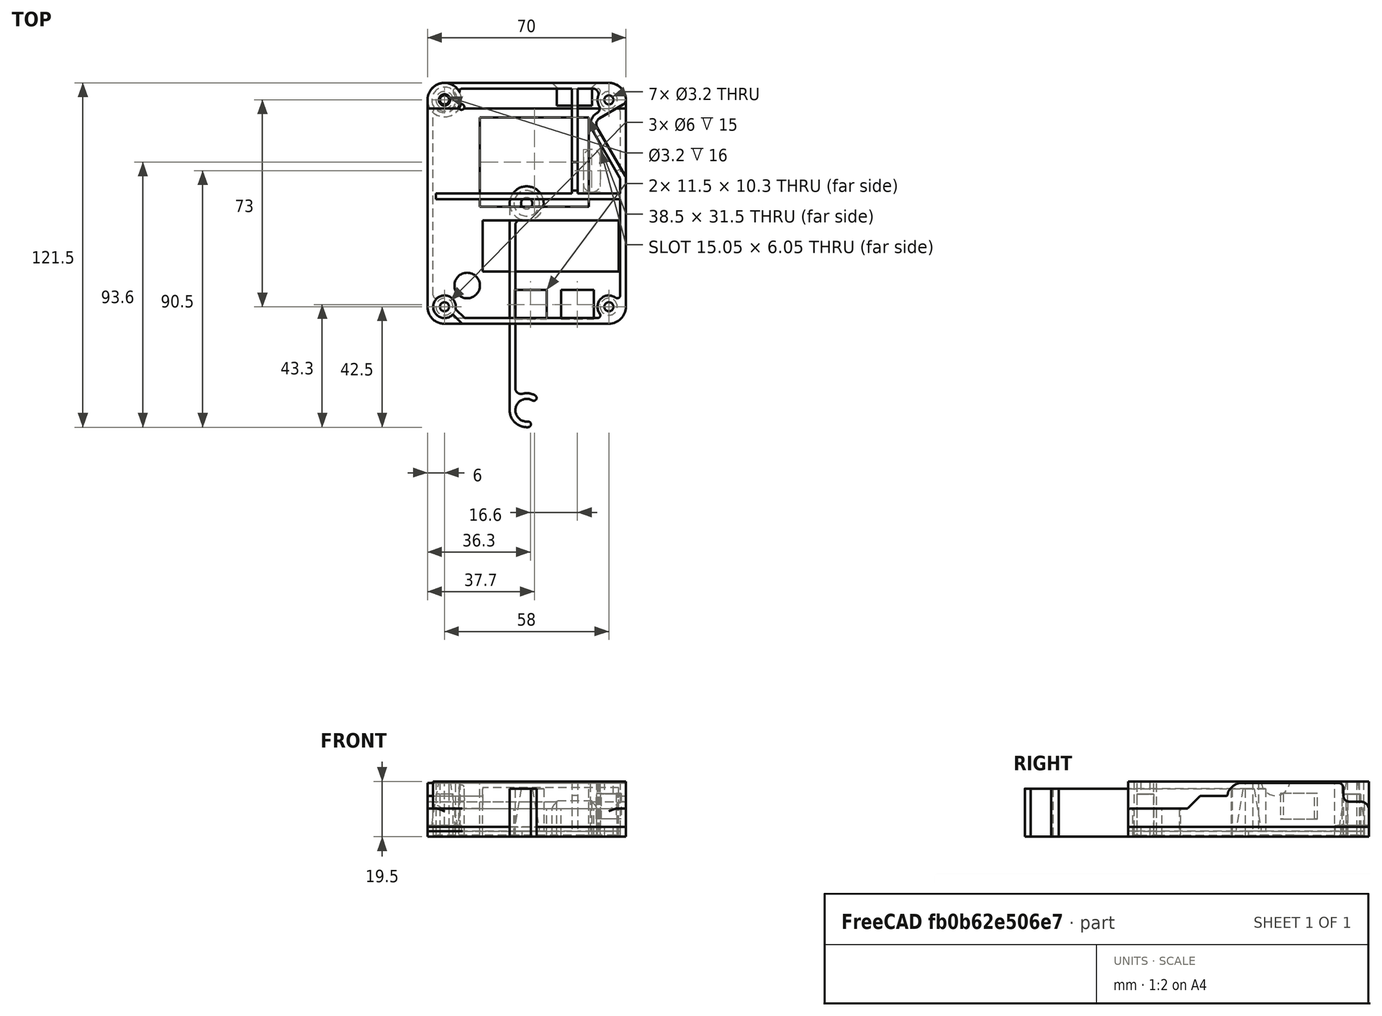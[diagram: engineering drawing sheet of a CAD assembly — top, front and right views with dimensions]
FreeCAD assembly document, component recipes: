
FREECAD ASSEMBLY — COMPONENT RECIPES ("GM328TesterCase")

This assembly document has 4 components, labeled P0..P3 below (a component is one placed body or linked part). 4 of them carry a construction recipe — the FreeCAD feature program that regenerates the part from scratch, quoted from this document or its linked companion documents; the rest are supplied as boundary geometry only. No exploded tour is included for this assembly.
COMPONENT P0 — recipe-attached ("Middle", modeled in this document).
Construction recipe (the document's own serialized feature program — sketch geometry with constraints, then the solid features built on it; lengths are millimeters unless a unit is written):

FEATURE [Sketcher::SketchObject] Sketch
  ArcFitTolerance = 1e-06
  AttachmentSupport = -> [XY_Plane]
  FullyConstrained = true
  MakeInternals = false
  MapMode = 5
  expr: Constraints[19] = <<Spreadsheet>>.OuterLength
  expr: Constraints[20] = <<Spreadsheet>>.OuterWidth
  expr: Constraints[21] = <<Spreadsheet>>.OuterCornerRadius
  expr: Constraints[29] = <<Spreadsheet>>.ThroughHole3
  sketch-geometry (18):
    g0: LineSegment StartX=-35 StartY=36.5 StartZ=0 EndX=-35 EndY=-36.5 EndZ=0
    g1: LineSegment StartX=-29 StartY=-42.5 StartZ=0 EndX=29 EndY=-42.5 EndZ=0
    g2: LineSegment StartX=35 StartY=-36.5 StartZ=0 EndX=35 EndY=36.5 EndZ=0
    g3: LineSegment StartX=29 StartY=42.5 StartZ=0 EndX=-29 EndY=42.5 EndZ=0
    g4: ArcOfCircle CenterX=-29 CenterY=36.5 CenterZ=0 NormalX=0 NormalY=0 NormalZ=1 AngleXU=0 Radius=6 StartAngle=1.5708 EndAngle=3.14159
    g5: ArcOfCircle CenterX=-29 CenterY=-36.5 CenterZ=0 NormalX=0 NormalY=0 NormalZ=1 AngleXU=0 Radius=6 StartAngle=3.14159 EndAngle=4.71239
    g6: ArcOfCircle CenterX=29 CenterY=-36.5 CenterZ=0 NormalX=0 NormalY=0 NormalZ=1 AngleXU=0 Radius=6 StartAngle=4.71239 EndAngle=6.28319
    g7: ArcOfCircle CenterX=29 CenterY=36.5 CenterZ=0 NormalX=0 NormalY=0 NormalZ=1 AngleXU=0 Radius=6 StartAngle=3e-16 EndAngle=1.5708
    g8: GeomPoint [constr] X=-35 Y=42.5 Z=0
    g9: GeomPoint [constr] X=35 Y=-42.5 Z=0
    g10: Circle CenterX=29 CenterY=36.5 CenterZ=0 NormalX=0 NormalY=0 NormalZ=1 AngleXU=0 Radius=1.6
    g11: Circle CenterX=-29 CenterY=36.5 CenterZ=0 NormalX=0 NormalY=0 NormalZ=1 AngleXU=0 Radius=1.6
    g12: Circle CenterX=-29 CenterY=-36.5 CenterZ=0 NormalX=0 NormalY=0 NormalZ=1 AngleXU=0 Radius=1.6
    g13: Circle CenterX=29 CenterY=-36.5 CenterZ=0 NormalX=0 NormalY=0 NormalZ=1 AngleXU=0 Radius=1.6
    g14: ArcOfCircle CenterX=23 CenterY=16 CenterZ=0 NormalX=0 NormalY=0 NormalZ=1 AngleXU=0 Radius=3.02394 StartAngle=3e-16 EndAngle=3.14159
    g15: ArcOfCircle CenterX=23 CenterY=7 CenterZ=0 NormalX=0 NormalY=0 NormalZ=1 AngleXU=0 Radius=3.02394 StartAngle=3.14159 EndAngle=6.28319
    g16: LineSegment StartX=26.0239 StartY=16 StartZ=0 EndX=26.0239 EndY=7 EndZ=0
    g17: LineSegment StartX=19.9761 StartY=16 StartZ=0 EndX=19.9761 EndY=7 EndZ=0
  constraints (40):
    c: Tangent(g0,g4) = -1.5708
    c: Tangent(g0,g5) = -1.5708
    c: Tangent(g1,g5) = -1.5708
    c: Tangent(g1,g6) = -1.5708
    c: Tangent(g2,g6) = -1.5708
    c: Tangent(g2,g7) = -1.5708
    c: Tangent(g3,g7) = -1.5708
    c: Tangent(g3,g4) = -1.5708
    c: Vertical(g2)
    c: Horizontal(g1)
    c: Equal(g4,g5)
    c: Equal(g5,g6)
    c: Equal(g6,g7)
    c: PointOnObject(g8,g0)
    c: PointOnObject(g8,g3)
    c: PointOnObject(g9,g1)
    c: PointOnObject(g9,g2)
    c: Symmetric(g3,g3,g-2)
    c: Symmetric(g0,g0,g-1)
    c: DistanceY(g1,g3) = 85
    c: DistanceX(g0,g2) = 70
    c: Radius(g7) = 6
    c: Coincident(g10,g7)
    c: Coincident(g11,g4)
    c: Coincident(g12,g5)
    c: Coincident(g13,g6)
    c: Equal(g13,g12)
    c: Equal(g12,g10)
    c: Equal(g10,g11)
    c: Diameter(g10) = 3.2
    c: Tangent(g14,g16) = 1.5708
    c: Tangent(g14,g17) = -1.5708
    c: Tangent(g15,g16) = 1.5708
    c: Tangent(g15,g17) = -1.5708
    c: Equal(g14,g15)
    c: Vertical(g17)
    c: Distance(g14) = 9.5
    c: DistanceY(g15,g14) = 9
    c: DistanceY(g15) = 7
    c: DistanceX(g15) = 23
FEATURE [PartDesign::Pad] Pad
  Direction = (0,0,1)
  Length = 3.5
  Length2 = 10
  Profile = -> Sketch
  ReferenceAxis = -> Sketch [N_Axis]
  Refine = true
  Suppressed = false
  Type = 0
FEATURE [Sketcher::SketchObject] Sketch001
  ArcFitTolerance = 1e-06
  AttachmentSupport = -> [Pad]
  ExternalGeometry = -> [Pad]
  FullyConstrained = true
  MakeInternals = false
  MapMode = 5
  Placement = pos=(0,0,3.5) rot=(0,0,1;0rad)
  expr: Constraints[33] = <<Spreadsheet>>.WallThickness
  expr: Constraints[34] = <<Spreadsheet>>.WallThickness
  expr: Constraints[35] = <<Spreadsheet>>.ScrewPostSmallRadius
  expr: Constraints[36] = <<Spreadsheet>>.ScrewPostDiameter / 2
  sketch-geometry (16):
    g0: LineSegment StartX=-33 StartY=-32.5 StartZ=0 EndX=-33 EndY=32.5 EndZ=0
    g1: LineSegment StartX=-25 StartY=40.5 StartZ=0 EndX=25 EndY=40.5 EndZ=0
    g2: LineSegment StartX=33 StartY=32.5 StartZ=0 EndX=33 EndY=-32.5 EndZ=0
    g3: LineSegment StartX=-25 StartY=-40.5 StartZ=0 EndX=25 EndY=-40.5 EndZ=0
    g4: ArcOfCircle CenterX=-32 CenterY=32.5 CenterZ=0 NormalX=0 NormalY=0 NormalZ=1 AngleXU=0 Radius=1 StartAngle=0.927295 EndAngle=3.14159
    g5: ArcOfCircle CenterX=-25 CenterY=39.5 CenterZ=0 NormalX=0 NormalY=0 NormalZ=1 AngleXU=0 Radius=1 StartAngle=1.5708 EndAngle=3.78509
    g6: ArcOfCircle CenterX=-29 CenterY=36.5 CenterZ=0 NormalX=0 NormalY=0 NormalZ=1 AngleXU=0 Radius=4 StartAngle=4.06889 EndAngle=6.92669
    g7: ArcOfCircle CenterX=25 CenterY=39.5 CenterZ=0 NormalX=0 NormalY=0 NormalZ=1 AngleXU=0 Radius=1 StartAngle=5.63967 EndAngle=7.85398
    g8: ArcOfCircle CenterX=32 CenterY=32.5 CenterZ=0 NormalX=0 NormalY=0 NormalZ=1 AngleXU=0 Radius=1 StartAngle=3.3e-15 EndAngle=2.2143
    g9: ArcOfCircle CenterX=29 CenterY=36.5 CenterZ=0 NormalX=0 NormalY=0 NormalZ=1 AngleXU=0 Radius=4 StartAngle=2.49809 EndAngle=5.35589
    g10: ArcOfCircle CenterX=32 CenterY=-32.5 CenterZ=0 NormalX=0 NormalY=0 NormalZ=1 AngleXU=0 Radius=1 StartAngle=4.06889 EndAngle=6.28319
    g11: ArcOfCircle CenterX=25 CenterY=-39.5 CenterZ=0 NormalX=0 NormalY=0 NormalZ=1 AngleXU=0 Radius=1 StartAngle=4.71239 EndAngle=6.92669
    g12: ArcOfCircle CenterX=29 CenterY=-36.5 CenterZ=0 NormalX=0 NormalY=0 NormalZ=1 AngleXU=0 Radius=4 StartAngle=0.927295 EndAngle=3.78509
    g13: ArcOfCircle CenterX=-25 CenterY=-39.5 CenterZ=0 NormalX=0 NormalY=0 NormalZ=1 AngleXU=0 Radius=1 StartAngle=2.49809 EndAngle=4.71239
    g14: ArcOfCircle CenterX=-32 CenterY=-32.5 CenterZ=0 NormalX=0 NormalY=0 NormalZ=1 AngleXU=0 Radius=1 StartAngle=3.14159 EndAngle=5.35589
    g15: ArcOfCircle CenterX=-29 CenterY=-36.5 CenterZ=0 NormalX=0 NormalY=0 NormalZ=1 AngleXU=0 Radius=4 StartAngle=5.63968 EndAngle=8.49748
  constraints (38):
    c: Vertical(g2)
    c: Horizontal(g3)
    c: Tangent(g13,g3) = -1.5708
    c: Tangent(g15,g13) = 1.5708
    c: Tangent(g15,g14) = 1.5708
    c: Tangent(g14,g0) = 1.5708
    c: Tangent(g4,g0) = 1.5708
    c: Tangent(g6,g4) = 1.5708
    c: Tangent(g6,g5) = 1.5708
    c: Tangent(g5,g1) = 1.5708
    c: Tangent(g8,g2) = 1.5708
    c: Tangent(g9,g8) = 1.5708
    c: Tangent(g10,g2) = 1.5708
    c: Tangent(g12,g10) = 1.5708
    c: Tangent(g12,g11) = 1.5708
    c: Tangent(g11,g3) = -1.5708
    c: Coincident(g9,g7)
    c: Tangent(g7,g1) = 1.5708
    c: Symmetric(g1,g1,g-2)
    c: Symmetric(g0,g0,g-1)
    c: Coincident(g6,g-3)
    c: Coincident(g9,g-6)
    c: Coincident(g12,g-7)
    c: Coincident(g-8,g15)
    c: Equal(g6,g9)
    c: Equal(g9,g12)
    c: Equal(g12,g15)
    c: Equal(g13,g14)
    c: Equal(g5,g4)
    c: Equal(g7,g8)
    c: Equal(g8,g11)
    c: Equal(g11,g10)
    c: Equal(g1,g3)
    c: DistanceY(g1,g-4) = 2
    c: DistanceX(g-5,g0) = 2
    c: Radius(g5) = 1
    c: Radius(g6) = 4
    c: Symmetric(g2,g0,g-2)
FEATURE [PartDesign::Pocket] Pocket
  BaseFeature = -> Pad
  Direction = (0,0,-1)
  Length = 0
  Length2 = 5
  Offset = -0.5
  Profile = -> Sketch001
  ReferenceAxis = -> Sketch001 [N_Axis]
  Refine = true
  Suppressed = false
  Type = 3
  UpToFace = -> Pad [Face17]
  expr: Offset = -<<Spreadsheet>>.MiddleBottomThickness
FEATURE [PartDesign::CoordinateSystem] Bottom  label="Bottom001"
  AttacherType = Attacher::AttachEngine3D
  AttachmentSupport = -> [Pocket]
  MapMode = 11
  Placement = pos=(29,36.5,0) rot=(0,0,1;1.5708rad)
FEATURE [PartDesign::Body] Body  label="Middle"
  AllowCompound = false
  Group = -> [Sketch,Pad,Sketch001,Pocket,Bottom]
  Origin = -> Origin
  Tip = -> Pocket
COMPONENT P1 — recipe-attached ("Bottom", modeled in this document).
Construction recipe (the document's own serialized feature program — sketch geometry with constraints, then the solid features built on it; lengths are millimeters unless a unit is written):

FEATURE [Sketcher::SketchObject] Sketch002
  ArcFitTolerance = 1e-06
  AttachmentSupport = -> [XY_Plane001]
  FullyConstrained = true
  MakeInternals = false
  MapMode = 5
  expr: Constraints[13] = <<Spreadsheet>>.OuterCornerRadius
  expr: Constraints[15] = <<Spreadsheet>>.OuterLength
  expr: Constraints[17] = <<Spreadsheet>>.OuterWidth
  expr: Constraints[40] = <<Spreadsheet>>.ThroughHole3
  sketch-geometry (19):
    g0: LineSegment StartX=-35 StartY=36.5 StartZ=0 EndX=-35 EndY=-36.5 EndZ=0
    g1: LineSegment StartX=-29 StartY=-42.5 StartZ=0 EndX=29 EndY=-42.5 EndZ=0
    g2: LineSegment StartX=29 StartY=42.5 StartZ=0 EndX=-29 EndY=42.5 EndZ=0
    g3: ArcOfCircle CenterX=-29 CenterY=36.5 CenterZ=0 NormalX=0 NormalY=0 NormalZ=1 AngleXU=0 Radius=6 StartAngle=1.5708 EndAngle=3.14159
    g4: ArcOfCircle CenterX=-29 CenterY=-36.5 CenterZ=0 NormalX=0 NormalY=0 NormalZ=1 AngleXU=0 Radius=6 StartAngle=3.14159 EndAngle=4.71239
    g5: ArcOfCircle CenterX=29 CenterY=-36.5 CenterZ=0 NormalX=0 NormalY=0 NormalZ=1 AngleXU=0 Radius=6 StartAngle=4.71239 EndAngle=6.28319
    g6: ArcOfCircle CenterX=29 CenterY=36.5 CenterZ=0 NormalX=0 NormalY=0 NormalZ=1 AngleXU=0 Radius=6 StartAngle=2.8032e-10 EndAngle=1.5708
    g7: GeomPoint [constr] X=-35 Y=42.5 Z=0
    g8: LineSegment StartX=35 StartY=-36.5 StartZ=0 EndX=35 EndY=8.8 EndZ=0
    g9: ArcOfCircle CenterX=33.1165 CenterY=36.5 CenterZ=0 NormalX=0 NormalY=0 NormalZ=1 AngleXU=0 Radius=1.88353 StartAngle=5.23599 EndAngle=6.28319
    g10: ArcOfCircle CenterX=33.1165 CenterY=8.8 CenterZ=0 NormalX=0 NormalY=0 NormalZ=1 AngleXU=0 Radius=1.88353 StartAngle=-1.69442e-10 EndAngle=0.523599
    g11: ArcOfCircle CenterX=27 CenterY=28 CenterZ=0 NormalX=0 NormalY=0 NormalZ=1 AngleXU=0 Radius=2.41945 StartAngle=2.0944 EndAngle=3.66519
    g12: LineSegment StartX=25.7903 StartY=30.0953 StartZ=0 EndX=34.0582 EndY=34.8688 EndZ=0
    g13: LineSegment StartX=24.9047 StartY=26.7903 StartZ=0 EndX=34.7477 EndY=9.74176 EndZ=0
    g14: LineSegment [constr] StartX=35 StartY=8.8 StartZ=0 EndX=35 EndY=36.5 EndZ=0
    g15: Circle CenterX=29 CenterY=36.5 CenterZ=0 NormalX=0 NormalY=0 NormalZ=1 AngleXU=0 Radius=1.6
    g16: Circle CenterX=29 CenterY=-36.5 CenterZ=0 NormalX=0 NormalY=0 NormalZ=1 AngleXU=0 Radius=1.6
    g17: Circle CenterX=-29 CenterY=-36.5 CenterZ=0 NormalX=0 NormalY=0 NormalZ=1 AngleXU=0 Radius=1.6
    g18: Circle CenterX=-29 CenterY=36.5 CenterZ=0 NormalX=0 NormalY=0 NormalZ=1 AngleXU=0 Radius=1.6
  constraints (43):
    c: Tangent(g0,g3) = -1.5708
    c: Tangent(g0,g4) = -1.5708
    c: Tangent(g1,g4) = -1.5708
    c: Tangent(g1,g5) = -1.5708
    c: Tangent(g2,g6) = -1.5708
    c: Tangent(g2,g3) = -1.5708
    c: Vertical(g0)
    c: Horizontal(g1)
    c: Horizontal(g2)
    c: Equal(g4,g5)
    c: Equal(g5,g6)
    c: PointOnObject(g7,g0)
    c: PointOnObject(g7,g2)
    c: Radius(g6) = 6
    c: Symmetric(g2,g1,g-1)
    c: DistanceY(g1,g2) = 85
    c: Tangent(g8,g5) = -1.5708
    c: DistanceX(g0,g5) = 70
    c: Symmetric(g0,g5,g-2)
    c: Equal(g1,g2)
    c: Tangent(g10,g8) = -1.5708
    c: Tangent(g13,g10) = 1.5708
    c: Tangent(g13,g11) = -1.5708
    c: Tangent(g12,g11) = 1.5708
    c: Tangent(g12,g9) = -1.5708
    c: Tangent(g9,g6) = -1.5708
    c: Tangent(g14,g6) = -1.5708
    c: Coincident(g14,g8)
    c: DistanceY(g8,g8) = 45.3
    c: Perpendicular(g12,g13)
    c: DistanceX(g11) = 27
    c: DistanceY(g11) = 28
    c: Angle(g13,g8) = 2.61799
    c: Equal(g10,g9)
    c: Coincident(g16,g5)
    c: Coincident(g17,g4)
    c: Coincident(g18,g3)
    c: Equal(g18,g15)
    c: Equal(g15,g16)
    c: Equal(g16,g17)
    c: Diameter(g15) = 3.2
    c: Coincident(g15,g6)
    c: DistanceY(g4,g3) = 73
FEATURE [PartDesign::Pad] Pad001
  Direction = (0,0,1)
  Length = 19.5
  Length2 = 10
  Profile = -> Sketch002
  ReferenceAxis = -> Sketch002 [N_Axis]
  Refine = true
  Suppressed = false
  Type = 0
  expr: Length = <<Spreadsheet>>.BottomTotalHeight
FEATURE [Sketcher::SketchObject] Sketch003
  ArcFitTolerance = 1e-06
  AttachmentSupport = -> [Pad001]
  ExternalGeometry = -> [Pad001]
  FullyConstrained = true
  MakeInternals = false
  MapMode = 5
  Placement = pos=(0,0,19.5) rot=(0,0,1;0rad)
  expr: Constraints[11] = <<Spreadsheet>>.WallThickness
  expr: Constraints[19] = <<Spreadsheet>>.WallThickness
  expr: Constraints[20] = <<Spreadsheet>>.WallThickness
  expr: Constraints[25] = <<Spreadsheet>>.ScrewPostSmallRadius
  expr: Constraints[31] = <<Spreadsheet>>.WallThickness
  expr: Constraints[44] = <<Spreadsheet>>.ScrewPostDiameter
  expr: Constraints[50] = <<Spreadsheet>>.WallThickness
  expr: Constraints[62] = <<Spreadsheet>>.ScrewPostSmallRadius
  expr: Constraints[6] = <<Spreadsheet>>.ScrewPostDiameter / 2
  expr: Constraints[78] = <<Spreadsheet>>.WallThickness
  expr: Constraints[79] = <<Spreadsheet>>.WallThickness
  expr: Constraints[8] = <<Spreadsheet>>.WallThickness
  sketch-geometry (35):
    g0: ArcOfCircle CenterX=29 CenterY=36.5 CenterZ=0 NormalX=0 NormalY=0 NormalZ=1 AngleXU=0 Radius=4 StartAngle=2.80176 EndAngle=3.65549
    g1: ArcOfCircle CenterX=23.775 CenterY=33.5506 CenterZ=0 NormalX=0 NormalY=0 NormalZ=1 AngleXU=0 Radius=2 StartAngle=5.23599 EndAngle=6.79708
    g2: ArcOfCircle CenterX=23.3431 CenterY=38.5 CenterZ=0 NormalX=0 NormalY=0 NormalZ=1 AngleXU=0 Radius=2 StartAngle=5.94335 EndAngle=7.85398
    g3: LineSegment StartX=23.3431 StartY=40.5 StartZ=0 EndX=18 EndY=40.5 EndZ=0
    g4: LineSegment StartX=23.1638 StartY=25.8056 StartZ=0 EndX=32.7321 EndY=9.23289 EndZ=0
    g5: LineSegment StartX=33 StartY=8.23289 StartZ=0 EndX=33 EndY=3.5 EndZ=0
    g6: ArcOfCircle CenterX=26.9759 CenterY=28.0065 CenterZ=0 NormalX=0 NormalY=0 NormalZ=1 AngleXU=0 Radius=4.40179 StartAngle=2.0944 EndAngle=3.66519
    g7: LineSegment [constr] StartX=24.775 StartY=31.8185 StartZ=0 EndX=20.9629 EndY=29.6176 EndZ=0
    g8: LineSegment [constr] StartX=23.1638 StartY=25.8056 StartZ=0 EndX=20.9629 EndY=29.6176 EndZ=0
    g9: ArcOfCircle CenterX=31 CenterY=8.23289 CenterZ=0 NormalX=0 NormalY=0 NormalZ=1 AngleXU=0 Radius=2 StartAngle=1e-16 EndAngle=0.523599
    g10: ArcOfCircle CenterX=29 CenterY=-36.5 CenterZ=0 NormalX=0 NormalY=0 NormalZ=1 AngleXU=0 Radius=4 StartAngle=0.927295 EndAngle=3.78509
    g11: ArcOfCircle CenterX=32 CenterY=-32.5 CenterZ=0 NormalX=0 NormalY=0 NormalZ=1 AngleXU=0 Radius=1 StartAngle=4.06889 EndAngle=6.28319
    g12: ArcOfCircle CenterX=25 CenterY=-39.5 CenterZ=0 NormalX=0 NormalY=0 NormalZ=1 AngleXU=0 Radius=1 StartAngle=4.71239 EndAngle=6.92669
    g13: LineSegment StartX=25 StartY=-40.5 StartZ=0 EndX=-21.8059 EndY=-40.5 EndZ=0
    g14: ArcOfCircle CenterX=-29 CenterY=-36.5 CenterZ=0 NormalX=0 NormalY=0 NormalZ=1 AngleXU=0 Radius=6 StartAngle=3.14159 EndAngle=4.71239
    g15: LineSegment StartX=-29 StartY=-42.5 StartZ=0 EndX=-22.6343 EndY=-42.5 EndZ=0
    g16: ArcOfCircle CenterX=-29 CenterY=-36.5 CenterZ=0 NormalX=0 NormalY=0 NormalZ=1 AngleXU=0 Radius=4 StartAngle=6.10603 EndAngle=11.781
    g17: ArcOfCircle CenterX=-22.6343 CenterY=-42.3 CenterZ=0 NormalX=0 NormalY=0 NormalZ=1 AngleXU=0 Radius=0.2 StartAngle=3.92699 EndAngle=4.71239
    g18: LineSegment StartX=-22.7757 StartY=-42.4414 StartZ=0 EndX=-25.8887 EndY=-39.3284 EndZ=0
    g19: ArcOfCircle CenterX=-26.0302 CenterY=-39.4698 CenterZ=0 NormalX=0 NormalY=0 NormalZ=1 AngleXU=0 Radius=0.2 StartAngle=0.785398 EndAngle=2.35619
    g20: ArcOfCircle CenterX=-21.8059 CenterY=-40.3 CenterZ=0 NormalX=0 NormalY=0 NormalZ=1 AngleXU=0 Radius=0.2 StartAngle=3.92699 EndAngle=4.71239
    g21: LineSegment StartX=-21.9473 StartY=-40.4414 StartZ=0 EndX=-25.0072 EndY=-37.3816 EndZ=0
    g22: ArcOfCircle CenterX=-24.8657 CenterY=-37.2402 CenterZ=0 NormalX=0 NormalY=0 NormalZ=1 AngleXU=0 Radius=0.2 StartAngle=2.96444 EndAngle=3.92699
    g23: LineSegment [constr] StartX=-26.1716 StartY=-39.3284 StartZ=0 EndX=-29.3339 EndY=-42.4907 EndZ=0
    g24: ArcOfCircle CenterX=-22.6754 CenterY=39.5 CenterZ=0 NormalX=0 NormalY=0 NormalZ=1 AngleXU=0 Radius=1 StartAngle=1.5708 EndAngle=3.5845
    g25: ArcOfCircle CenterX=-29 CenterY=36.5 CenterZ=0 NormalX=0 NormalY=0 NormalZ=1 AngleXU=0 Radius=6 StartAngle=3.14159 EndAngle=6.7261
    g26: LineSegment StartX=-35 StartY=-36.5 StartZ=0 EndX=-35 EndY=36.5 EndZ=0
    g27: LineSegment StartX=16 StartY=40.5 StartZ=0 EndX=16 EndY=3.5 EndZ=0
    g28: LineSegment StartX=18 StartY=40.5 StartZ=0 EndX=18 EndY=3.5 EndZ=0
    g29: LineSegment StartX=18 StartY=3.5 StartZ=0 EndX=33 EndY=3.5 EndZ=0
    g30: LineSegment StartX=33 StartY=1.5 StartZ=0 EndX=-32 EndY=1.5 EndZ=0
    g31: LineSegment StartX=-32 StartY=1.5 StartZ=0 EndX=-32 EndY=3.5 EndZ=0
    g32: LineSegment StartX=-32 StartY=3.5 StartZ=0 EndX=16 EndY=3.5 EndZ=0
    g33: LineSegment StartX=33 StartY=1.5 StartZ=0 EndX=33 EndY=-32.5 EndZ=0
    g34: LineSegment StartX=16 StartY=40.5 StartZ=0 EndX=-22.6754 EndY=40.5 EndZ=0
  constraints (93):
    c: Horizontal(g3)
    c: Tangent(g2,g0) = 1.5708
    c: Tangent(g3,g2) = -1.5708
    c: Tangent(g1,g0) = 1.5708
    c: Vertical(g5)
    c: Equal(g1,g2)
    c: Radius(g0) = 4
    c: Coincident(g0,g-9)
    c: DistanceY(g2,g-3) = 2
    c: Radius(g2) = 2
    c: Parallel(g4,g-7)
    c: Distance(g-7,g4) = 2
    c: Tangent(g6,g4) = -1.5708
    c: Tangent(g6,g1) = 1.5708
    c: Coincident(g8,g4)
    c: Coincident(g8,g7)
    c: Tangent(g7,g1) = 1.5708
    c: Perpendicular(g7,g8)
    c: Parallel(g4,g8)
    c: Distance(g-12,g7) = 2
    c: DistanceX(g5,g-6) = 2
    c: Tangent(g9,g5) = 1.5708
    c: Tangent(g9,g4) = 1.5708
    c: Equal(g1,g9)
    c: Equal(g11,g12)
    c: Radius(g11) = 1
    c: Equal(g0,g10)
    c: Tangent(g12,g10) = 1.5708
    c: Tangent(g11,g10) = 1.5708
    c: Coincident(g10,g-11)
    c: Horizontal(g13)
    c: DistanceY(g-5,g12) = 2
    c: Tangent(g13,g12) = 1.5708
    c: Coincident(g14,g-4)
    c: Coincident(g14,g-5)
    c: Equal(g14,g-13)
    c: Tangent(g14,g15) = -1.5708
    c: Coincident(g16,g14)
    c: Tangent(g17,g15) = -1.5708
    c: Tangent(g18,g17) = 1.5708
    c: Tangent(g19,g18) = -1.5708
    c: Tangent(g19,g16) = 1.5708
    c: Equal(g17,g19)
    c: Radius(g19) = 0.2
    c: Diameter(g16) = 8
    c: Tangent(g20,g13) = 1.5708
    c: Tangent(g21,g20) = 1.5708
    c: Equal(g20,g19)
    c: Angle(g18,g15) = 0.785398
    c: Parallel(g18,g21)
    c: Distance(g20,g18) = 2
    c: Tangent(g22,g21) = 1.5708
    c: Tangent(g22,g16) = 1.5708
    c: Equal(g20,g22)
    c: Coincident(g23,g16)
    c: PointOnObject(g23,g14)
    c: Tangent(g19,g23)
    c: Perpendicular(g18,g23)
    c: Coincident(g25,g-14)
    c: PointOnObject(g25,g-4)
    c: Equal(g25,g-15)
    c: Tangent(g25,g24) = 1.5708
    c: Radius(g24) = 1
    c: Coincident(g26,g14)
    c: Coincident(g26,g25)
    c: PointOnObject(g27,g34)
    c: Vertical(g27)
    c: Vertical(g28)
    c: Coincident(g29,g28)
    c: Horizontal(g29)
    c: PointOnObject(g30,g33)
    c: Horizontal(g30)
    c: Coincident(g31,g30)
    c: Vertical(g31)
    c: Coincident(g32,g31)
    c: Coincident(g32,g27)
    c: Horizontal(g32)
    c: Horizontal(g27,g28)
    c: DistanceX(g27,g28) = 2
    c: DistanceY(g31,g31) = 2
    c: DistanceX(g25,g31) = 3
    c: DistanceY(g30,g-15) = 41
    c: DistanceX(g27,g30) = 17
    c: Coincident(g5,g29)
    c: PointOnObject(g33,g30)
    c: Coincident(g3,g28)
    c: PointOnObject(g34,g27)
    c: Vertical(g33)
    c: Vertical(g30,g5)
    c: Horizontal(g34)
    c: Horizontal(g27,g3)
    c: Tangent(g24,g34) = -1.5708
    c: Tangent(g11,g33) = 1.5708
FEATURE [PartDesign::Pocket] Pocket001
  BaseFeature = -> Pad001
  Direction = (0,0,-1)
  Length = 0
  Length2 = 5
  Offset = -2
  Profile = -> Sketch003
  ReferenceAxis = -> Sketch003 [N_Axis]
  Refine = true
  Suppressed = false
  Type = 3
  UpToFace = -> Pad001 [Face18]
  expr: Offset = -<<Spreadsheet>>.BottomBottomThickness
FEATURE [PartDesign::Line] DatumLine
  AttacherType = Attacher::AttachEngineLine
  AttachmentSupport = -> [Pocket001]
  Length = 20
  MapMode = 19
  Placement = pos=(-29,36.5,19.5) rot=(0,0,1;0rad)
  ResizeMode = 0
FEATURE [Sketcher::SketchObject] Sketch004
  ArcFitTolerance = 1e-06
  AttachmentSupport = -> [DatumLine]
  ExternalGeometry = -> [Pocket001]
  FullyConstrained = true
  MakeInternals = false
  MapMode = 3
  Placement = pos=(-29,36.5,19.5) rot=(1,0,0;1.5708rad)
  expr: Constraints[12] = <<Spreadsheet>>.CoverSwivelBottomDiameter / 2
  expr: Constraints[8] = <<Spreadsheet>>.BottomBottomThickness + <<Spreadsheet>>.CoverSwivelZCutout
  expr: Constraints[9] = <<Spreadsheet>>.CoverSwivelTopDiameter / 2
  sketch-geometry (4):
    g0: LineSegment StartX=-6 StartY=0 StartZ=0 EndX=-6 EndY=-15.5 EndZ=0
    g1: LineSegment StartX=-6 StartY=-15.5 StartZ=0 EndX=-4.5 EndY=-15.5 EndZ=0
    g2: LineSegment StartX=-4.5 StartY=-15.5 StartZ=0 EndX=-2 EndY=0 EndZ=0
    g3: LineSegment StartX=-2 StartY=0 StartZ=0 EndX=-6 EndY=0 EndZ=0
  constraints (13):
    c: Coincident(g-3,g0)
    c: Vertical(g0)
    c: Coincident(g0,g1)
    c: Horizontal(g1)
    c: Coincident(g1,g2)
    c: PointOnObject(g2,g-3)
    c: Coincident(g2,g3)
    c: Coincident(g3,g0)
    c: DistanceY(g-4,g0) = 4
    c: DistanceX(g2,g-1) = 2
    c: DistanceX(g1,g1) = 1.5
    c: Angle(g0,g2) = 2.98168  'CoverSwivelAngle'
    c: DistanceX(g1,g-1) = 4.5
FEATURE [PartDesign::Groove] Groove
  Angle = 360
  Angle2 = 60
  Axis = (0,2e-16,1)
  Base = (-29,36.5,19.5)
  BaseFeature = -> Pocket001
  Profile = -> Sketch004
  ReferenceAxis = -> Sketch004 [V_Axis]
  Refine = true
  Reversed = true
  Suppressed = false
  Type = 0
FEATURE [Sketcher::SketchObject] Sketch005
  ArcFitTolerance = 1e-06
  AttachmentSupport = -> [Groove]
  ExternalGeometry = -> [Groove]
  FullyConstrained = true
  MakeInternals = false
  MapMode = 5
  Placement = pos=(0,0,0) rot=(1,0,0;3.14159rad)
  expr: Constraints[5] = <<Spreadsheet>>.CounterboreDiameter
  sketch-geometry (3):
    g0: Circle CenterX=29 CenterY=-36.5 CenterZ=0 NormalX=0 NormalY=0 NormalZ=1 AngleXU=0 Radius=3
    g1: Circle CenterX=29 CenterY=36.5 CenterZ=0 NormalX=0 NormalY=0 NormalZ=1 AngleXU=0 Radius=3
    g2: Circle CenterX=-29 CenterY=36.5 CenterZ=0 NormalX=0 NormalY=0 NormalZ=1 AngleXU=0 Radius=3
  constraints (6):
    c: Coincident(g0,g-5)
    c: Coincident(g1,g-4)
    c: Coincident(g2,g-3)
    c: Equal(g1,g2)
    c: Equal(g2,g0)
    c: Diameter(g1) = 6
FEATURE [PartDesign::Pocket] Pocket002
  BaseFeature = -> Groove
  Direction = (0,0,1)
  Length = 15
  Length2 = 5
  Profile = -> Sketch005
  ReferenceAxis = -> Sketch005 [N_Axis]
  Refine = true
  Suppressed = false
  Type = 0
  expr: Length = <<Spreadsheet>>.CounterboreDepth1
FEATURE [Sketcher::SketchObject] Sketch006
  ArcFitTolerance = 1e-06
  AttachmentSupport = -> [Pocket002]
  ExternalGeometry = -> [Pocket002]
  FullyConstrained = true
  MakeInternals = false
  MapMode = 5
  Placement = pos=(0,0,0) rot=(1,0,0;3.14159rad)
  expr: Constraints[1] = <<Spreadsheet>>.CounterboreDiameter
  sketch-geometry (1):
    g0: Circle CenterX=-29 CenterY=-36.5 CenterZ=0 NormalX=0 NormalY=0 NormalZ=1 AngleXU=0 Radius=3
  constraints (2):
    c: Coincident(g0,g-3)
    c: Diameter(g0) = 6
FEATURE [PartDesign::Pocket] Pocket003
  BaseFeature = -> Pocket002
  Direction = (0,0,1)
  Length = 3.5
  Length2 = 5
  Profile = -> Sketch006
  ReferenceAxis = -> Sketch006 [N_Axis]
  Refine = true
  Suppressed = false
  Type = 0
  expr: Length = <<Spreadsheet>>.CounterboreDepth2
FEATURE [Sketcher::SketchObject] Sketch007
  ArcFitTolerance = 1e-06
  AttachmentSupport = -> [Pocket003]
  ExternalGeometry = -> [Pocket003]
  FullyConstrained = true
  MakeInternals = false
  MapMode = 5
  Placement = pos=(16,0,0) rot=(0.57735,-0.57735,-0.57735;2.0944rad)
  sketch-geometry (2):
    g0: ArcOfCircle CenterX=-9.5 CenterY=19.5 CenterZ=0 NormalX=0 NormalY=0 NormalZ=1 AngleXU=0 Radius=5 StartAngle=3.14159 EndAngle=6.28319
    g1: LineSegment StartX=-14.5 StartY=19.5 StartZ=0 EndX=-4.5 EndY=19.5 EndZ=0
  constraints (7):
    c: PointOnObject(g0,g-3)
    c: PointOnObject(g0,g-3)
    c: PointOnObject(g0,g-3)
    c: Diameter(g0) = 10
    c: DistanceX(g0,g-3) = 1
    c: Coincident(g1,g0)
    c: Coincident(g1,g0)
FEATURE [PartDesign::Pocket] Pocket004
  BaseFeature = -> Pocket003
  Direction = (1,0,0)
  Length = 5
  Length2 = 5
  Profile = -> Sketch007
  ReferenceAxis = -> Sketch007 [N_Axis]
  Refine = true
  Suppressed = false
  Type = 2
FEATURE [Sketcher::SketchObject] Sketch008
  ArcFitTolerance = 1e-06
  AttachmentSupport = -> [Pocket004]
  ExternalGeometry = -> [Pocket004]
  FullyConstrained = true
  MakeInternals = false
  MapMode = 5
  Placement = pos=(30.279,17.4816,0) rot=(0.377964,0.654654,0.654654;2.41886rad)
  sketch-geometry (7):
    g0: LineSegment StartX=-6.09425 StartY=15.25 StartZ=0 EndX=-6.09425 EndY=6.25 EndZ=0
    g1: LineSegment StartX=-6.09425 StartY=6.25 StartZ=0 EndX=7.90575 EndY=6.25 EndZ=0
    g2: LineSegment StartX=7.90575 StartY=6.25 StartZ=0 EndX=7.90575 EndY=15.25 EndZ=0
    g3: LineSegment StartX=7.90575 StartY=15.25 StartZ=0 EndX=-6.09425 EndY=15.25 EndZ=0
    g4: GeomPoint [constr] X=0.905749 Y=10.75 Z=0
    g5: LineSegment [constr] StartX=0.905749 StartY=10.75 StartZ=0 EndX=0.905749 EndY=19.5 EndZ=0
    g6: LineSegment [constr] StartX=0.905749 StartY=10.75 StartZ=0 EndX=0.905749 EndY=2 EndZ=0
  constraints (18):
    c: Coincident(g0,g1)
    c: Coincident(g1,g2)
    c: Coincident(g2,g3)
    c: Coincident(g3,g0)
    c: Vertical(g0)
    c: Vertical(g2)
    c: Horizontal(g1)
    c: Horizontal(g3)
    c: Symmetric(g2,g0,g4)
    c: DistanceX(g3,g3) = 14
    c: DistanceY(g2,g2) = 9
    c: Coincident(g5,g4)
    c: Vertical(g5)
    c: Coincident(g6,g4)
    c: Vertical(g6)
    c: Equal(g5,g6)
    c: PointOnObject(g6,g-3)
    c: Symmetric(g-4,g-4,g5)
FEATURE [PartDesign::Pocket] Pocket005
  BaseFeature = -> Pocket004
  Direction = (-0.866025,-0.5,-1e-16)
  Length = 5
  Length2 = 5
  Profile = -> Sketch008
  ReferenceAxis = -> Sketch008 [N_Axis]
  Refine = true
  Suppressed = false
  Type = 2
FEATURE [PartDesign::CoordinateSystem] Mount
  AttacherType = Attacher::AttachEngine3D
  AttachmentSupport = -> [Pocket005]
  MapMode = 11
  Placement = pos=(-29,-36.5,0) rot=(0.707107,-0.707107,0;3.14159rad)
FEATURE [PartDesign::CoordinateSystem] Cover  label="Cover001"
  AttacherType = Attacher::AttachEngine3D
  AttachmentSupport = -> [Pocket005]
  MapMode = 11
  Placement = pos=(-29,36.5,19.5) rot=(0,0,1;1.5708rad)
FEATURE [PartDesign::CoordinateSystem] Middle  label="Middle001"
  AttacherType = Attacher::AttachEngine3D
  AttachmentSupport = -> [Pocket005]
  MapMode = 11
  Placement = pos=(29,36.5,19.5) rot=(0,0,1;1.5708rad)
FEATURE [PartDesign::Body] Body001  label="Bottom"
  AllowCompound = false
  Group = -> [Sketch002,Pad001,Sketch003,Pocket001,DatumLine,Sketch004,Groove,Sketch005,Pocket002,Sketch006,Pocket003,Sketch007,Pocket004,Sketch008,Pocket005,Mount,Cover,Middle]
  Origin = -> Origin001
  Tip = -> Pocket005
COMPONENT P2 — recipe-attached ("Cover", modeled in this document).
Construction recipe (the document's own serialized feature program — sketch geometry with constraints, then the solid features built on it; lengths are millimeters unless a unit is written):

FEATURE [Sketcher::SketchObject] Sketch009
  ArcFitTolerance = 1e-06
  AttachmentSupport = -> [XY_Plane002]
  FullyConstrained = true
  MakeInternals = false
  MapMode = 5
  expr: Constraints[13] = <<Spreadsheet>>.OuterCornerRadius
  expr: Constraints[17] = <<Spreadsheet>>.WallThickness
  expr: Constraints[18] = <<Spreadsheet>>.OuterLength - <<Spreadsheet>>.OuterCornerRadius * 2
  expr: Constraints[20] = <<Spreadsheet>>.WallThickness
  expr: Constraints[26] = <<Spreadsheet>>.CoverSwivelTopDiameter
  sketch-geometry (11):
    g0: ArcOfCircle CenterX=0 CenterY=0 CenterZ=0 NormalX=0 NormalY=0 NormalZ=1 AngleXU=0 Radius=6 StartAngle=4.45971 EndAngle=9.42478
    g1: LineSegment StartX=-6 StartY=2.2e-15 StartZ=0 EndX=-6 EndY=-73 EndZ=0
    g2: LineSegment StartX=-4 StartY=-65.254 StartZ=0 EndX=-4 EndY=-7.74597 EndZ=0
    g3: ArcOfCircle CenterX=-2 CenterY=-7.74597 CenterZ=0 NormalX=0 NormalY=0 NormalZ=1 AngleXU=0 Radius=2 StartAngle=1.31812 EndAngle=3.14159
    g4: ArcOfCircle CenterX=-2 CenterY=-65.254 CenterZ=0 NormalX=0 NormalY=0 NormalZ=1 AngleXU=0 Radius=2 StartAngle=3.14159 EndAngle=4.96507
    g5: ArcOfCircle CenterX=0 CenterY=-73 CenterZ=0 NormalX=0 NormalY=0 NormalZ=1 AngleXU=0 Radius=6 StartAngle=1.0472 EndAngle=1.82348
    g6: ArcOfCircle CenterX=2.5 CenterY=-68.6699 CenterZ=0 NormalX=0 NormalY=0 NormalZ=1 AngleXU=0 Radius=1 StartAngle=4.18879 EndAngle=7.33038
    g7: ArcOfCircle CenterX=0 CenterY=-73 CenterZ=0 NormalX=0 NormalY=0 NormalZ=1 AngleXU=0 Radius=4 StartAngle=1.0472 EndAngle=4.81256
    g8: ArcOfCircle CenterX=0.5 CenterY=-77.9749 CenterZ=0 NormalX=0 NormalY=0 NormalZ=1 AngleXU=0 Radius=1 StartAngle=4.81256 EndAngle=7.95415
    g9: ArcOfCircle CenterX=0 CenterY=-73 CenterZ=0 NormalX=0 NormalY=0 NormalZ=1 AngleXU=0 Radius=6 StartAngle=3.14159 EndAngle=4.81256
    g10: Circle CenterX=0 CenterY=0 CenterZ=0 NormalX=0 NormalY=0 NormalZ=1 AngleXU=0 Radius=2
  constraints (27):
    c: Coincident(g0,g-1)
    c: Vertical(g1)
    c: Vertical(g2)
    c: Tangent(g4,g2) = 1.5708
    c: Tangent(g5,g4) = 1.5708
    c: Tangent(g6,g5) = -1.5708
    c: Tangent(g7,g6) = 1.5708
    c: Tangent(g8,g7) = 1.5708
    c: Tangent(g9,g8) = -1.5708
    c: Tangent(g9,g1) = -1.5708
    c: Tangent(g1,g0) = -1.5708
    c: Tangent(g3,g0) = 1.5708
    c: Tangent(g3,g2) = 1.5708
    c: Radius(g0) = 6
    c: Radius(g3) = 2
    c: PointOnObject(g7,g-2)
    c: Equal(g4,g3)
    c: DistanceX(g1,g2) = 2
    c: DistanceY(g7,g0) = 73
    c: Equal(g8,g6)
    c: Diameter(g6) = 2
    c: Coincident(g9,g7)
    c: Coincident(g9,g5)
    c: DistanceX(g8) = 0.5
    c: DistanceX(g6) = 2.5
    c: Coincident(g10,g0)
    c: Diameter(g10) = 4
FEATURE [PartDesign::Pad] Pad002
  Direction = (0,0,1)
  Length = 17
  Length2 = 10
  Profile = -> Sketch009
  ReferenceAxis = -> Sketch009 [N_Axis]
  Refine = true
  Suppressed = false
  Type = 0
  expr: Length = <<Spreadsheet>>.CoverHeight
FEATURE [Sketcher::SketchObject] Sketch010
  ArcFitTolerance = 1e-06
  AttachmentSupport = -> [YZ_Plane002]
  ExternalGeometry = -> [Pad002]
  FullyConstrained = true
  MakeInternals = false
  MapMode = 5
  Placement = pos=(0,0,0) rot=(0.57735,0.57735,0.57735;2.0944rad)
  expr: Constraints[12] = <<Spreadsheet>>.CoverSwivelZCutout
  expr: Constraints[13] = <<Spreadsheet>>.CoverSwivelBottomDiameter / 2
  sketch-geometry (6):
    g0: LineSegment StartX=0 StartY=17 StartZ=0 EndX=2 EndY=17 EndZ=0
    g1: LineSegment StartX=2 StartY=17 StartZ=0 EndX=4.5 EndY=2 EndZ=0
    g2: LineSegment StartX=4.5 StartY=2 StartZ=0 EndX=6 EndY=2 EndZ=0
    g3: LineSegment StartX=6 StartY=2 StartZ=0 EndX=6 EndY=0 EndZ=0
    g4: LineSegment StartX=6 StartY=0 StartZ=0 EndX=0 EndY=0 EndZ=0
    g5: LineSegment StartX=0 StartY=0 StartZ=0 EndX=0 EndY=17 EndZ=0
  constraints (14):
    c: Symmetric(g-3,g-3,g0)
    c: Coincident(g0,g-3)
    c: Coincident(g0,g1)
    c: Coincident(g1,g2)
    c: Coincident(g2,g3)
    c: Coincident(g3,g4)
    c: Coincident(g4,g-1)
    c: Coincident(g4,g5)
    c: Coincident(g5,g0)
    c: Vertical(g3)
    c: Coincident(g-4,g3)
    c: Horizontal(g2)
    c: DistanceY(g3,g3) = 2
    c: DistanceX(g1) = 4.5
FEATURE [PartDesign::Groove] Groove001
  Angle = 360
  Angle2 = 60
  Axis = (0,0,1)
  Base = (0,0,0)
  BaseFeature = -> Pad002
  Profile = -> Sketch010
  ReferenceAxis = -> Sketch010 [V_Axis]
  Refine = true
  Suppressed = false
  Type = 0
FEATURE [PartDesign::CoordinateSystem] Bottom001  label="Bottom002"
  AttacherType = Attacher::AttachEngine3D
  AttachmentOffset = pos=(0,0,0) rot=(0,0,1;2.0944rad)
  AttachmentSupport = -> [Groove001]
  MapMode = 11
  Placement = pos=(0,0,17) rot=(0,0,1;5.23599rad)
FEATURE [PartDesign::Body] Body002  label="Cover"
  AllowCompound = false
  Group = -> [Sketch009,Pad002,Sketch010,Groove001,Bottom001]
  Origin = -> Origin002
  Tip = -> Groove001
COMPONENT P3 — recipe-attached ("Top", modeled in this document).
Construction recipe (the document's own serialized feature program — sketch geometry with constraints, then the solid features built on it; lengths are millimeters unless a unit is written):

FEATURE [Sketcher::SketchObject] Sketch011
  ArcFitTolerance = 1e-06
  AttachmentSupport = -> [XY_Plane004]
  FullyConstrained = true
  MakeInternals = false
  MapMode = 5
  expr: Constraints[18] = <<Spreadsheet>>.OuterLength
  expr: Constraints[19] = <<Spreadsheet>>.OuterWidth
  expr: Constraints[20] = <<Spreadsheet>>.OuterCornerRadius
  expr: Constraints[21] = <<Spreadsheet>>.LEDHoleX
  expr: Constraints[22] = <<Spreadsheet>>.LEDHoleY
  expr: Constraints[23] = <<Spreadsheet>>.LEDHoleDiameter
  expr: Constraints[33] = <<Spreadsheet>>.DisplayWidth
  expr: Constraints[34] = <<Spreadsheet>>.DisplayHeight
  expr: Constraints[35] = <<Spreadsheet>>.DisplayX
  expr: Constraints[36] = <<Spreadsheet>>.DisplayY
  expr: Constraints[46] = <<Spreadsheet>>.ZIFWidth
  expr: Constraints[47] = <<Spreadsheet>>.ZIFHeight
  expr: Constraints[48] = <<Spreadsheet>>.ZIFX
  expr: Constraints[49] = <<Spreadsheet>>.ZIFY
  expr: Constraints[50] = <<Spreadsheet>>.REDiameter
  expr: Constraints[51] = <<Spreadsheet>>.REX
  expr: Constraints[52] = <<Spreadsheet>>.REY
  sketch-geometry (38):
    g0: LineSegment StartX=-35 StartY=36.5 StartZ=0 EndX=-35 EndY=-36.5 EndZ=0
    g1: LineSegment StartX=-29 StartY=-42.5 StartZ=0 EndX=29 EndY=-42.5 EndZ=0
    g2: LineSegment StartX=35 StartY=-36.5 StartZ=0 EndX=35 EndY=36.5 EndZ=0
    g3: LineSegment StartX=29 StartY=42.5 StartZ=0 EndX=24.7 EndY=42.5 EndZ=0
    g4: ArcOfCircle CenterX=-29 CenterY=36.5 CenterZ=0 NormalX=0 NormalY=0 NormalZ=1 AngleXU=0 Radius=6 StartAngle=1.5708 EndAngle=3.14159
    g5: ArcOfCircle CenterX=-29 CenterY=-36.5 CenterZ=0 NormalX=0 NormalY=0 NormalZ=1 AngleXU=0 Radius=6 StartAngle=3.14159 EndAngle=4.71239
    g6: ArcOfCircle CenterX=29 CenterY=-36.5 CenterZ=0 NormalX=0 NormalY=0 NormalZ=1 AngleXU=0 Radius=6 StartAngle=4.71239 EndAngle=6.28319
    g7: ArcOfCircle CenterX=29 CenterY=36.5 CenterZ=0 NormalX=0 NormalY=0 NormalZ=1 AngleXU=0 Radius=6 StartAngle=3e-16 EndAngle=1.5708
    g8: GeomPoint [constr] X=-35 Y=42.5 Z=0
    g9: GeomPoint [constr] X=35 Y=-42.5 Z=0
    g10: Circle CenterX=-23 CenterY=34 CenterZ=0 NormalX=0 NormalY=0 NormalZ=1 AngleXU=0 Radius=1
    g11: LineSegment StartX=-16.55 StartY=30.35 StartZ=0 EndX=-16.55 EndY=-1.15 EndZ=0
    g12: LineSegment StartX=-16.55 StartY=-1.15 StartZ=0 EndX=21.95 EndY=-1.15 EndZ=0
    g13: LineSegment StartX=21.95 StartY=-1.15 StartZ=0 EndX=21.95 EndY=30.35 EndZ=0
    g14: LineSegment StartX=21.95 StartY=30.35 StartZ=0 EndX=-16.55 EndY=30.35 EndZ=0
    g15: GeomPoint [constr] X=2.7 Y=14.6 Z=0
    g16: LineSegment StartX=-15.5 StartY=-6 StartZ=0 EndX=-15.5 EndY=-24 EndZ=0
    g17: LineSegment StartX=-15.5 StartY=-24 StartZ=0 EndX=32.5 EndY=-24 EndZ=0
    g18: LineSegment StartX=32.5 StartY=-24 StartZ=0 EndX=32.5 EndY=-6 EndZ=0
    g19: LineSegment StartX=32.5 StartY=-6 StartZ=0 EndX=-15.5 EndY=-6 EndZ=0
    g20: GeomPoint [constr] X=8.5 Y=-15 Z=0
    g21: Circle CenterX=-21 CenterY=-29 CenterZ=0 NormalX=0 NormalY=0 NormalZ=1 AngleXU=0 Radius=4.5
    g22: LineSegment StartX=-4.45 StartY=-30.55 StartZ=0 EndX=-4.45 EndY=-40.85 EndZ=0
    g23: LineSegment StartX=-4.45 StartY=-40.85 StartZ=0 EndX=7.05 EndY=-40.85 EndZ=0
    g24: LineSegment StartX=7.05 StartY=-40.85 StartZ=0 EndX=7.05 EndY=-30.55 EndZ=0
    g25: LineSegment StartX=7.05 StartY=-30.55 StartZ=0 EndX=-4.45 EndY=-30.55 EndZ=0
    g26: GeomPoint [constr] X=1.3 Y=-35.7 Z=0
    g27: LineSegment StartX=12.15 StartY=-30.55 StartZ=0 EndX=12.15 EndY=-40.85 EndZ=0
    g28: LineSegment StartX=12.15 StartY=-40.85 StartZ=0 EndX=23.65 EndY=-40.85 EndZ=0
    g29: LineSegment StartX=23.65 StartY=-40.85 StartZ=0 EndX=23.65 EndY=-30.55 EndZ=0
    g30: LineSegment StartX=23.65 StartY=-30.55 StartZ=0 EndX=12.15 EndY=-30.55 EndZ=0
    g31: GeomPoint [constr] X=17.9 Y=-35.7 Z=0
    g32: LineSegment StartX=9 StartY=42.5 StartZ=0 EndX=10.6 EndY=40.9 EndZ=0
    g33: LineSegment StartX=10.6 StartY=40.9 StartZ=0 EndX=10.6 EndY=34.5 EndZ=0
    g34: LineSegment StartX=10.6 StartY=34.5 StartZ=0 EndX=23.1 EndY=34.5 EndZ=0
    g35: LineSegment StartX=23.1 StartY=34.5 StartZ=0 EndX=23.1 EndY=40.9 EndZ=0
    g36: LineSegment StartX=23.1 StartY=40.9 StartZ=0 EndX=24.7 EndY=42.5 EndZ=0
    g37: LineSegment StartX=9 StartY=42.5 StartZ=0 EndX=-29 EndY=42.5 EndZ=0
  constraints (99):
    c: Tangent(g0,g4) = -1.5708
    c: Tangent(g0,g5) = -1.5708
    c: Tangent(g1,g5) = -1.5708
    c: Tangent(g1,g6) = -1.5708
    c: Tangent(g2,g6) = -1.5708
    c: Tangent(g2,g7) = -1.5708
    c: Tangent(g3,g7) = -1.5708
    c: Vertical(g0)
    c: Vertical(g2)
    c: Horizontal(g1)
    c: Horizontal(g3)
    c: Equal(g5,g6)
    c: PointOnObject(g8,g0)
    c: PointOnObject(g8,g37)
    c: PointOnObject(g9,g1)
    c: PointOnObject(g9,g2)
    c: Symmetric(g37,g1,g-1)
    c: Symmetric(g0,g2,g-2)
    c: DistanceY(g1,g37) = 85
    c: DistanceX(g0,g2) = 70
    c: Radius(g4) = 6
    c: DistanceX(g10,g-1) = 23
    c: DistanceY(g10) = 34
    c: Diameter(g10) = 2
    c: Coincident(g11,g12)
    c: Coincident(g12,g13)
    c: Coincident(g13,g14)
    c: Coincident(g14,g11)
    c: Vertical(g11)
    c: Vertical(g13)
    c: Horizontal(g12)
    c: Horizontal(g14)
    c: Symmetric(g13,g11,g15)
    c: DistanceX(g14,g14) = 38.5
    c: DistanceY(g11,g11) = 31.5
    c: DistanceX(g15) = 2.7
    c: DistanceY(g15) = 14.6
    c: Coincident(g16,g17)
    c: Coincident(g17,g18)
    c: Coincident(g18,g19)
    c: Coincident(g19,g16)
    c: Vertical(g16)
    c: Vertical(g18)
    c: Horizontal(g17)
    c: Horizontal(g19)
    c: Symmetric(g18,g16,g20)
    c: DistanceX(g17,g17) = 48
    c: DistanceY(g16,g16) = 18
    c: DistanceX(g20) = 8.5
    c: DistanceY(g20,g-1) = 15
    c: Diameter(g21) = 9
    c: DistanceX(g21,g-1) = 21
    c: DistanceY(g21,g-1) = 29
    c: Coincident(g22,g23)
    c: Coincident(g23,g24)
    c: Coincident(g24,g25)
    c: Coincident(g25,g22)
    c: Vertical(g22)
    c: Vertical(g24)
    c: Horizontal(g23)
    c: Horizontal(g25)
    c: Symmetric(g24,g22,g26)
    c: Coincident(g27,g28)
    c: Coincident(g28,g29)
    c: Coincident(g29,g30)
    c: Coincident(g30,g27)
    c: Vertical(g27)
    c: Vertical(g29)
    c: Horizontal(g28)
    c: Horizontal(g30)
    c: Symmetric(g29,g27,g31)
    c: PointOnObject(g32,g37)
    c: Coincident(g32,g33)
    c: Vertical(g33)
    c: Coincident(g33,g34)
    c: Horizontal(g34)
    c: Coincident(g34,g35)
    c: Vertical(g35)
    c: Coincident(g35,g36)
    c: Coincident(g3,g36)
    c: PointOnObject(g37,g32)
    c: Angle(g37,g32) = 2.35619
    c: Perpendicular(g36,g32)
    c: Equal(g36,g32)
    c: DistanceX(g23,g23) = 11.5
    c: Equal(g23,g28)
    c: Horizontal(g31,g26)
    c: DistanceY(g22,g22) = 10.3
    c: DistanceX(g-1,g26) = 1.3
    c: DistanceY(g26,g-1) = 35.7
    c: Equal(g27,g24)
    c: DistanceX(g26,g31) = 16.6
    c: Equal(g7,g4)
    c: Equal(g4,g5)
    c: DistanceX(g34,g34) = 12.5
    c: Tangent(g37,g4) = -1.5708
    c: DistanceY(g33,g32) = 8
    c: DistanceX(g32) = 9
    c: DistanceY(g35,g35) = 6.4
FEATURE [PartDesign::Pad] Pad003
  Direction = (0,0,1)
  Length = 19
  Length2 = 10
  Profile = -> Sketch011
  ReferenceAxis = -> Sketch011 [N_Axis]
  Refine = true
  Suppressed = false
  Type = 0
FEATURE [Sketcher::SketchObject] Sketch012
  ArcFitTolerance = 1e-06
  AttachmentSupport = -> [Pad003]
  ExternalGeometry = -> [Pad003]
  FullyConstrained = false
  MakeInternals = false
  MapMode = 5
  Placement = pos=(-35,0,0) rot=(0.57735,-0.57735,-0.57735;2.0944rad)
  sketch-geometry (22):
    g0: LineSegment StartX=-42.5 StartY=19 StartZ=0 EndX=-31.5 EndY=19 EndZ=0
    g1: LineSegment StartX=21.3464 StartY=10.1464 StartZ=0 EndX=17.2393 EndY=14.2536 EndZ=0
    g2: LineSegment StartX=42.5 StartY=9 StartZ=0 EndX=42.5 EndY=19 EndZ=0
    g3: ArcOfCircle CenterX=41.5 CenterY=9 CenterZ=0 NormalX=0 NormalY=0 NormalZ=1 AngleXU=0 Radius=1 StartAngle=7e-16 EndAngle=1.5708
    g4: LineSegment StartX=41.5 StartY=10 StartZ=0 EndX=21.7 EndY=10 EndZ=0
    g5: LineSegment StartX=16.8858 StartY=14.4 StartZ=0 EndX=7.88579 EndY=14.4 EndZ=0
    g6: LineSegment StartX=-35.5 StartY=12.4 StartZ=0 EndX=-39.5 EndY=12.4 EndZ=0
    g7: LineSegment StartX=-42.5 StartY=9.4 StartZ=0 EndX=-42.5 EndY=19 EndZ=0
    g8: LineSegment StartX=2.5 StartY=19 StartZ=0 EndX=42.5 EndY=19 EndZ=0
    g9: ArcOfCircle CenterX=16.8858 CenterY=13.9 CenterZ=0 NormalX=0 NormalY=0 NormalZ=1 AngleXU=0 Radius=0.5 StartAngle=0.785398 EndAngle=1.5708
    g10: GeomPoint [constr] X=17.0929 Y=14.4 Z=0
    g11: GeomPoint [constr] X=7.56361 Y=14.4 Z=0
    g12: ArcOfCircle CenterX=-35.5 CenterY=14.4 CenterZ=0 NormalX=0 NormalY=0 NormalZ=1 AngleXU=0 Radius=2 StartAngle=4.71239 EndAngle=6.28319
    g13: ArcOfCircle CenterX=-31.5 CenterY=17 CenterZ=0 NormalX=0 NormalY=0 NormalZ=1 AngleXU=0 Radius=2 StartAngle=1.5708 EndAngle=3.14159
    g14: LineSegment StartX=-33.5 StartY=14.4 StartZ=0 EndX=-33.5 EndY=17 EndZ=0
    g15: ArcOfCircle CenterX=-39.5 CenterY=9.4 CenterZ=0 NormalX=0 NormalY=0 NormalZ=1 AngleXU=0 Radius=3 StartAngle=1.5708 EndAngle=3.14159
    g16: ArcOfCircle CenterX=2.5 CenterY=14.5 CenterZ=0 NormalX=0 NormalY=0 NormalZ=1 AngleXU=0 Radius=4.5 StartAngle=0.785398 EndAngle=1.5708
    g17: LineSegment StartX=6.51117 StartY=16.8528 StartZ=0 EndX=5.68198 EndY=17.682 EndZ=0
    g18: ArcOfCircle CenterX=21.7 CenterY=10.5 CenterZ=0 NormalX=0 NormalY=0 NormalZ=1 AngleXU=0 Radius=0.5 StartAngle=3.92699 EndAngle=4.71239
    g19: GeomPoint [constr] X=21.5293 Y=9.9636 Z=0
    g20: ArcOfCircle CenterX=4.38985 CenterY=14.7315 CenterZ=0 NormalX=0 NormalY=0 NormalZ=1 AngleXU=0 Radius=3 StartAngle=0.0481688 EndAngle=0.785398
    g21: ArcOfCircle CenterX=7.88579 CenterY=14.9 CenterZ=0 NormalX=0 NormalY=0 NormalZ=1 AngleXU=0 Radius=0.5 StartAngle=3.18976 EndAngle=4.71239
  constraints (51):
    c: Coincident(g8,g-3)
    c: Coincident(g2,g8)
    c: Vertical(g2)
    c: Tangent(g3,g2) = -1.5708
    c: Horizontal(g4)
    c: Tangent(g4,g3) = -1.5708
    c: DistanceY(g3) = 10
    c: Radius(g3) = 1
    c: Horizontal(g6)
    c: PointOnObject(g7,g-4)
    c: Coincident(g7,g0)
    c: Coincident(g0,g-4)
    c: Horizontal(g8)
    c: Horizontal(g5)
    c: PointOnObject(g10,g1)
    c: PointOnObject(g10,g5)
    c: Tangent(g1,g9) = -1.5708
    c: Tangent(g5,g9) = -1.5708
    c: PointOnObject(g11,g5)
    c: Tangent(g6,g12) = 1.5708
    c: Horizontal(g0)
    c: Tangent(g14,g12) = -1.5708
    c: Tangent(g14,g13) = 1.5708
    c: Tangent(g13,g0) = 1.5708
    c: Vertical(g14)
    c: Tangent(g16,g8) = 1.5708
    c: Tangent(g17,g16) = -1.5708
    c: PointOnObject(g19,g1)
    c: Tangent(g1,g18) = 1.5708
    c: DistanceX(g8,g8) = 40
    c: Angle(g5,g17) = 2.35619
    c: Tangent(g20,g17) = -1.5708
    c: Tangent(g21,g20) = 1.5708
    c: Angle(g4,g1) = 2.35619
    c: Radius(g18) = 0.5
    c: Equal(g18,g9)
    c: DistanceY(g5) = 14.4
    c: Tangent(g4,g18) = 1.5708
    c: DistanceX(g4,g4) = 19.8
    c: Tangent(g5,g21) = 1.5708
    c: Equal(g9,g21)
    c: Radius(g20) = 3
    c: Radius(g16) = 4.5
    c: DistanceX(g5,g5) = 9
    c: Tangent(g15,g7) = 1.5708
    c: DistanceY(g6,g0) = 6.6
    c: DistanceX(g0,g0) = 11
    c: Radius(g13) = 2
    c: Equal(g12,g13)
    c: Tangent(g6,g15) = -1.5708
    c: Radius(g15) = 3
FEATURE [PartDesign::Pocket] Pocket006
  BaseFeature = -> Pad003
  Direction = (1,0,0)
  Length = 5
  Length2 = 5
  Profile = -> Sketch012
  ReferenceAxis = -> Sketch012 [N_Axis]
  Refine = true
  Suppressed = false
  Type = 1
FEATURE [PartDesign::Body] Body003  label="Top"
  AllowCompound = false
  Group = -> [Sketch011,Pad003,Sketch012,Pocket006]
  Origin = -> Origin004
  Tip = -> Pocket006
PROVENANCE & LICENSES
A FreeCAD (.FCStd) document from a public repository crawl; recipes are the document's own serialized feature recipes (and, for linked parts, companion documents' recipes).
License: as declared in the source repository (recorded in the dataset sidecar).
